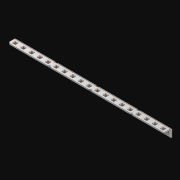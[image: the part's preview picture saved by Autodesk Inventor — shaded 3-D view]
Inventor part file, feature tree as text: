
AUTODESK INVENTOR PART (.ipt)
format: ipt  version: 2021 (Build 250183000, 183)  size: 711,680 bytes
history: native  units: in
note: dims shown in document units (in); Inventor stores cm internally (conversion verified against a paired STEP export)
features: extrude x39, other x38, sketch x3, pattern_linear x1, sheet_metal_op x1
ambient origin geometry x8: Origin, YZ Plane, XZ Plane, XY Plane, X Axis, Y Axis, Z Axis, Center Point
bodies: Solid1 (feature_tree)
feature tree (82):
  pattern_linear  "Rectangular Pattern1"  Spacing1=0.063in  [1 undecoded]
  extrude  "Extrusion1"  Depth=0.5in
  sketch  "Sketch1"  dims[d0=0.182in]
  other  "Srf1"
  sketch  "Sketch2"  dims[d1=0.063in d2=0.0in]
  other  "Srf2"
  other  "Srf3"
  other  "Srf5"
  other  "Srf7"
  other  "Srf9"
  other  "Srf11"
  other  "Srf13"
  other  "Srf15"
  other  "Srf17"
  other  "Srf19"
  other  "Srf21"
  other  "Srf23"
  other  "Srf25"
  other  "Srf27"
  other  "Srf29"
  other  "Srf31"
  other  "Srf33"
  other  "Srf35"
  other  "Srf37"
  other  "Srf4"
  other  "Srf6"
  other  "Srf8"
  other  "Srf10"
  other  "Srf12"
  other  "Srf14"
  other  "Srf16"
  other  "Srf18"
  other  "Srf20"
  other  "Srf22"
  other  "Srf24"
  other  "Srf26"
  other  "Srf28"
  other  "Srf30"
  other  "Srf32"
  other  "Srf34"
  other  "Srf36"
  other  "Srf38"
  sketch  "Sketch3"  dims[d3=0.182in d4=0.063in d5=0.0in d8=0.5in d9=8.0in d10=0.0in]
  sheet_metal_op  "Fold1"
  extrude  "ExtrusionSrf1"  Depth=8.0in TaperAngle=0.0deg
  extrude  "ExtrusionSrf2"  [1 undecoded]
  extrude  "ExtrusionSrf3"  [1 undecoded]
  extrude  "ExtrusionSrf4"  [1 undecoded]
  extrude  "ExtrusionSrf5"  [1 undecoded]
  extrude  "ExtrusionSrf6"  [1 undecoded]
  extrude  "ExtrusionSrf7"  [1 undecoded]
  extrude  "ExtrusionSrf8"  [1 undecoded]
  extrude  "ExtrusionSrf9"  [1 undecoded]
  extrude  "ExtrusionSrf10"  [1 undecoded]
  extrude  "ExtrusionSrf11"  [1 undecoded]
  extrude  "ExtrusionSrf12"  [1 undecoded]
  extrude  "ExtrusionSrf13"  [1 undecoded]
  extrude  "ExtrusionSrf14"  [1 undecoded]
  extrude  "ExtrusionSrf15"  [1 undecoded]
  extrude  "ExtrusionSrf16"  [1 undecoded]
  extrude  "ExtrusionSrf17"  [1 undecoded]
  extrude  "ExtrusionSrf18"  [1 undecoded]
  extrude  "ExtrusionSrf19"  [1 undecoded]
  extrude  "ExtrusionSrf20"  [1 undecoded]
  extrude  "ExtrusionSrf37"  [1 undecoded]
  extrude  "ExtrusionSrf38"  [1 undecoded]
  extrude  "ExtrusionSrf39"  [1 undecoded]
  extrude  "ExtrusionSrf40"  [1 undecoded]
  extrude  "ExtrusionSrf41"  [1 undecoded]
  extrude  "ExtrusionSrf42"  [1 undecoded]
  extrude  "ExtrusionSrf43"  [1 undecoded]
  extrude  "ExtrusionSrf44"  [1 undecoded]
  extrude  "ExtrusionSrf45"  [1 undecoded]
  extrude  "ExtrusionSrf46"  [1 undecoded]
  extrude  "ExtrusionSrf47"  [1 undecoded]
  extrude  "ExtrusionSrf48"  [1 undecoded]
  extrude  "ExtrusionSrf49"  [1 undecoded]
  extrude  "ExtrusionSrf50"  [1 undecoded]
  extrude  "ExtrusionSrf51"  [1 undecoded]
  extrude  "ExtrusionSrf52"  [1 undecoded]
  extrude  "ExtrusionSrf53"  [1 undecoded]
  extrude  "ExtrusionSrf54"  [1 undecoded]
note: 38 required parameter values undecoded (feature->parameter linkage not recoverable at this tier; creation-order binding heuristic only, values carry confidence <= 0.55)
